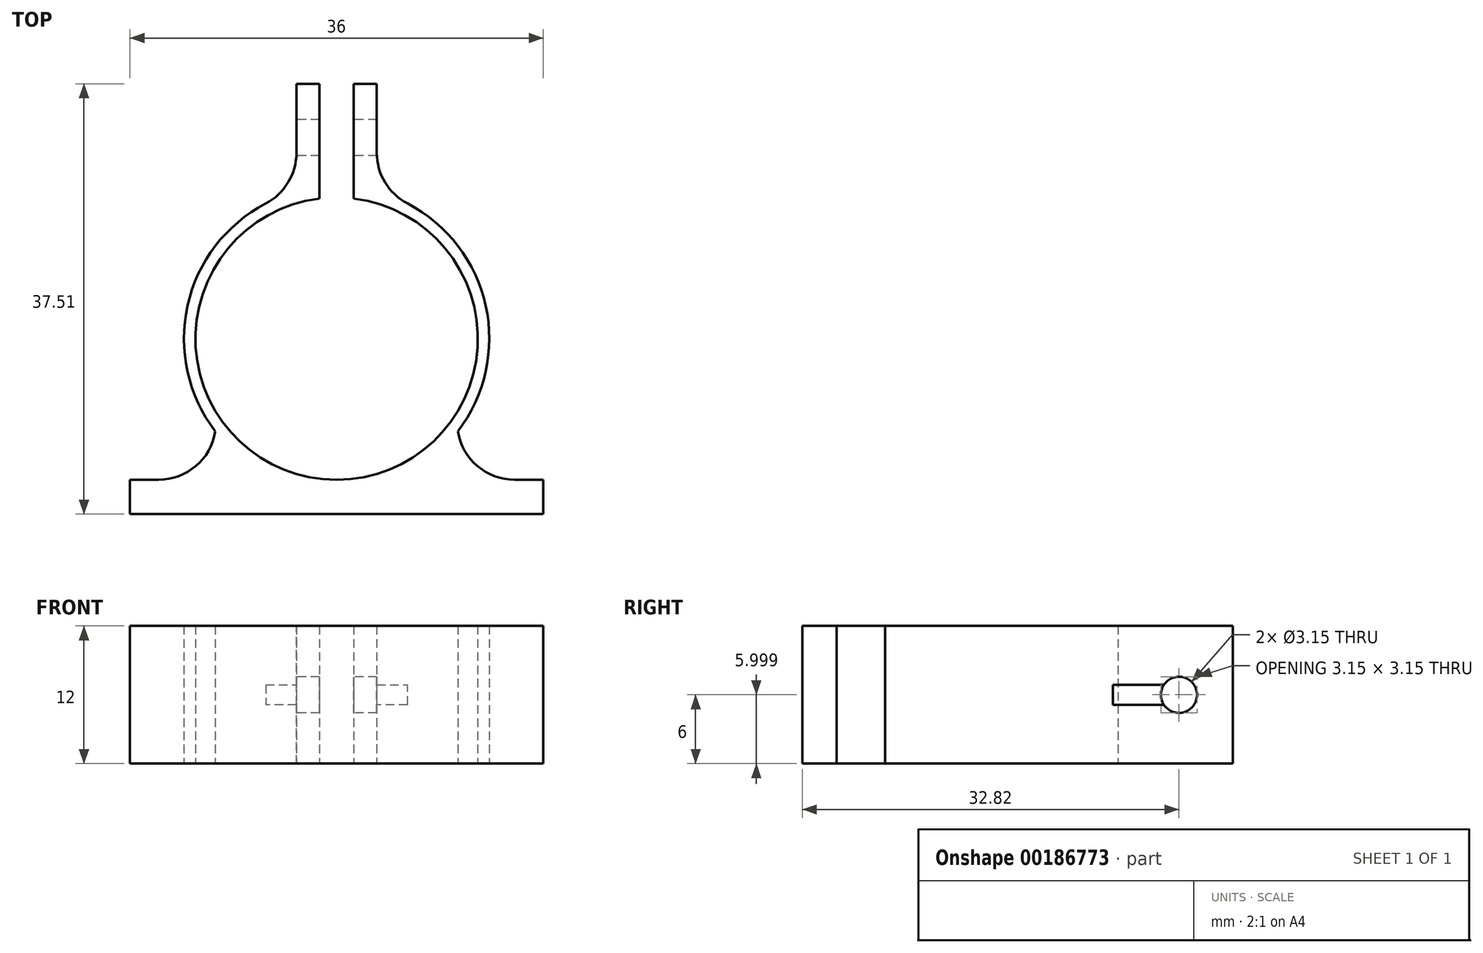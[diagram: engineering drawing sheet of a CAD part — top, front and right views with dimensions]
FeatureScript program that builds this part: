
annotation { "Feature Type Name" : "Feature", "Feature Type Description" : "" }
export const myFeature = defineFeature(function(context is Context, id is Id, definition is map)
    precondition{}
    {
        {
            var Q0;
            Q0=qCreatedBy(makeId("Top.planeOp"),FACE);
            var sketch = newSketch(context, id + "F0", { "sketchPlane" : qUnion([Q0])});
            skCircle(sketch, "E0", {"center": v(0, 0) * mm, "radius": 12.3 * mm});
            skLineSegment(sketch, "E1.bottom", {"start": v(0, -12.3) * mm, "end": v(18, -12.3) * mm});
            skLineSegment(sketch, "E1.top", {"start": v(0, -15.3) * mm, "end": v(18, -15.3) * mm});
            skLineSegment(sketch, "E1.right", {"start": v(18, -12.3) * mm, "end": v(18, -15.3) * mm});
            skLineSegment(sketch, "E2.bottom", {"start": v(0, -12.3) * mm, "end": v(-18, -12.3) * mm});
            skLineSegment(sketch, "E2.top", {"start": v(0, -15.3) * mm, "end": v(-18, -15.3) * mm});
            skLineSegment(sketch, "E2.right", {"start": v(-18, -12.3) * mm, "end": v(-18, -15.3) * mm});
            skCircle(sketch, "E3", {"center": v(0, 0) * mm, "radius": 13.3 * mm});
            skLineSegment(sketch, "E4", {"start": v(-10.56, -12.3) * mm, "end": v(-10.56, -6.3) * mm});
            skLineSegment(sketch, "E5", {"start": v(10.56, -12.3) * mm, "end": v(10.56, -6.3) * mm});
            skLineSegment(sketch, "E6", {"start": v(0, 29.14) * mm, "end": v(0, 0) * mm, "construction": true});
            skLineSegment(sketch, "E7.bottom", {"start": v(1.5, 22.2) * mm, "end": v(-1.5, 22.2) * mm, "construction": true});
            skLineSegment(sketch, "E7.left", {"start": v(1.5, 22.2) * mm, "end": v(1.5, 12.2) * mm});
            skLineSegment(sketch, "E7.right", {"start": v(-1.5, 22.2) * mm, "end": v(-1.5, 12.2) * mm});
            skPoint(sketch, "E7.middle", {"position": v(0, 13.3) * mm});
            skLineSegment(sketch, "E8.bottom", {"start": v(-1.5, 22.2) * mm, "end": v(-3.5, 22.2) * mm});
            skLineSegment(sketch, "E8.top", {"start": v(-1.5, 12.2) * mm, "end": v(-3.5, 12.2) * mm});
            skLineSegment(sketch, "E8.right", {"start": v(-3.5, 22.2) * mm, "end": v(-3.5, 12.2) * mm});
            skLineSegment(sketch, "E9.bottom", {"start": v(1.5, 22.2) * mm, "end": v(3.5, 22.2) * mm});
            skLineSegment(sketch, "E9.top", {"start": v(1.5, 12.2) * mm, "end": v(3.5, 12.2) * mm});
            skLineSegment(sketch, "E9.right", {"start": v(3.5, 22.2) * mm, "end": v(3.5, 12.2) * mm});
            skLineSegment(sketch, "E10", {"start": v(0, 0) * mm, "end": v(0, -22.28) * mm, "construction": true});
            skSolve(sketch);
        }
        {
            var Q0;
            {var subQ0=sQuery(id+"F0.wireOp",EDGE,"E8.top");Q0=makeQuery(id+"F0.imprint","IMPRINT",FACE,{"disambiguationData":[TD([[makeQuery(id+"F0.imprint","IMPRINT",EDGE,{"derivedFrom":subQ0}),1.0]])]});}
            var Q1;
            {var subQ5=sQuery(id+"F0.wireOp",EDGE,"E8.bottom");Q1=makeQuery(id+"F0.imprint","IMPRINT",FACE,{"disambiguationData":[TD([[makeQuery(id+"F0.imprint","IMPRINT",EDGE,{"derivedFrom":subQ5}),1.0]])]});}
            var Q2;
            {var subQ5=sQuery(id+"F0.wireOp",EDGE,"E8.top");Q2=makeQuery(id+"F0.imprint","IMPRINT",FACE,{"disambiguationData":[TD([[makeQuery(id+"F0.imprint","IMPRINT",EDGE,{"derivedFrom":subQ5}),-1.0]])]});}
            var Q3;
            {var subQ5=sQuery(id+"F0.wireOp",EDGE,"E9.bottom");Q3=makeQuery(id+"F0.imprint","IMPRINT",FACE,{"disambiguationData":[TD([[makeQuery(id+"F0.imprint","IMPRINT",EDGE,{"derivedFrom":subQ5}),-1.0]])]});}
            var Q4;
            {var subQ5=sQuery(id+"F0.wireOp",EDGE,"E9.top");Q4=makeQuery(id+"F0.imprint","IMPRINT",FACE,{"disambiguationData":[TD([[makeQuery(id+"F0.imprint","IMPRINT",EDGE,{"derivedFrom":subQ5}),1.0]])]});}
            var Q5;
            {var subQ5=sQuery(id+"F0.wireOp",EDGE,"E9.top");Q5=makeQuery(id+"F0.imprint","IMPRINT",FACE,{"disambiguationData":[TD([[makeQuery(id+"F0.imprint","IMPRINT",EDGE,{"derivedFrom":subQ5}),-1.0]])]});}
            var Q6;
            {var subQ3=sQuery(id+"F0.wireOp",EDGE,"E4");var subQ5=sQuery(id+"F0.wireOp",EDGE,"E3");var subQ7=makeQuery(id+"F0.imprint","INTERSECT",VERTEX,{"derivedFrom":[subQ5,subQ3]});Q6=makeQuery(id+"F0.imprint","IMPRINT",FACE,{"disambiguationData":[TD([[makeQuery(id+"F0.imprint","IMPRINT",EDGE,{"disambiguationData":[TD([[subQ7,-1.0]])],"derivedFrom":subQ5}),1.0]])]});}
            var Q7;
            {var subQ1=sQuery(id+"F0.wireOp",EDGE,"E1.bottom");var subQ3=sQuery(id+"F0.wireOp",EDGE,"E3");var subQ4=makeQuery(id+"F0.imprint","INTERSECT",VERTEX,{"derivedFrom":[subQ1,subQ3]});Q7=makeQuery(id+"F0.imprint","IMPRINT",FACE,{"disambiguationData":[TD([[makeQuery(id+"F0.imprint","IMPRINT",EDGE,{"disambiguationData":[TD([[subQ4,1.0]])],"derivedFrom":subQ3}),1.0]])]});}
            var Q8;
            {var subQ3=sQuery(id+"F0.wireOp",EDGE,"E5");var subQ5=sQuery(id+"F0.wireOp",EDGE,"E3");var subQ7=makeQuery(id+"F0.imprint","INTERSECT",VERTEX,{"derivedFrom":[subQ5,subQ3]});Q8=makeQuery(id+"F0.imprint","IMPRINT",FACE,{"disambiguationData":[TD([[makeQuery(id+"F0.imprint","IMPRINT",EDGE,{"disambiguationData":[TD([[subQ7,1.0]])],"derivedFrom":subQ5}),1.0]])]});}
            var Q9;
            {var subQ0=sQuery(id+"F0.wireOp",EDGE,"E5");var subQ1=sQuery(id+"F0.wireOp",EDGE,"E1.bottom");var subQ2=makeQuery(id+"F0.imprint","INTERSECT",VERTEX,{"derivedFrom":[subQ1,subQ0]});Q9=makeQuery(id+"F0.imprint","IMPRINT",FACE,{"disambiguationData":[TD([[makeQuery(id+"F0.imprint","IMPRINT",EDGE,{"disambiguationData":[TD([[subQ2,1.0]])],"derivedFrom":subQ1}),1.0]])]});}
            var Q10;
            {var subQ0=sQuery(id+"F0.wireOp",EDGE,"E4");var subQ1=sQuery(id+"F0.wireOp",EDGE,"E2.bottom");var subQ2=makeQuery(id+"F0.imprint","INTERSECT",VERTEX,{"derivedFrom":[subQ1,subQ0]});Q10=makeQuery(id+"F0.imprint","IMPRINT",FACE,{"disambiguationData":[TD([[makeQuery(id+"F0.imprint","IMPRINT",EDGE,{"disambiguationData":[TD([[subQ2,1.0]])],"derivedFrom":subQ1}),-1.0]])]});}
            var Q11;
            Q11=makeQuery(id+"F0.imprint","IMPRINT",FACE,{"disambiguationData":[TD([[makeQuery(id+"F0.imprint","IMPRINT",EDGE,{"derivedFrom":sQuery(id+"F0.wireOp",EDGE,"E1.top")}),1.0]])]});
            extrude(context, id + "F1", {"entities" : qUnion([Q0, Q1, Q2, Q3, Q4, Q5, Q6, Q7, Q8, Q9, Q10, Q11]), "depth" : 12 * mm});
        }
        {
            var Q0;
            Q0=makeQuery(id+"F1.opExtrude","SWEPT_FACE",FACE,{"disambiguationData":[OSD([sQuery(id+"F0.wireOp",EDGE,"E8.right")])]});
            var sketch = newSketch(context, id + "F2", { "sketchPlane" : qUnion([Q0])});
            skLineSegment(sketch, "E11", {"start": v(-22.2, 12) * mm, "end": v(-12.83, 0) * mm, "construction": true});
            skPoint(sketch, "E12", {"position": v(-17.52, 6) * mm});
            skSolve(sketch);
        }
        {
            var Q0;
            Q0=sQuery(id+"F2.wireOp",VERTEX,"E12");
            var Q1;
            Q1=makeQuery(id+"F1.opExtrude","SWEPT_BODY",BODY,{"disambiguationData":[OSD([sQuery(id+"F0.wireOp",EDGE,"E0"),sQuery(id+"F0.wireOp",EDGE,"E1.bottom"),sQuery(id+"F0.wireOp",EDGE,"E1.top"),sQuery(id+"F0.wireOp",EDGE,"E1.right"),sQuery(id+"F0.wireOp",EDGE,"E2.bottom"),sQuery(id+"F0.wireOp",EDGE,"E2.top"),sQuery(id+"F0.wireOp",EDGE,"E2.right"),sQuery(id+"F0.wireOp",EDGE,"E3"),sQuery(id+"F0.wireOp",EDGE,"E4"),sQuery(id+"F0.wireOp",EDGE,"E5"),sQuery(id+"F0.wireOp",EDGE,"E8.bottom"),sQuery(id+"F0.wireOp",EDGE,"E7.right"),sQuery(id+"F0.wireOp",EDGE,"E8.right"),sQuery(id+"F0.wireOp",EDGE,"E9.bottom"),sQuery(id+"F0.wireOp",EDGE,"E7.left"),sQuery(id+"F0.wireOp",EDGE,"E9.right")])]});
            hole(context, id + "F3", {"style" : HoleStyle.SIMPLE, "endStyle" : HoleEndStyle.THROUGH, "holeDiameter" : 3.15 * mm, "startFromSketch" : true, "locations" : qUnion([Q0]), "scope" : qUnion([Q1]), "isTappedThrough" : true});
        }
        {
            var Q0;
            Q0=makeQuery(id+"F1.opExtrude","SWEPT_EDGE",EDGE,{"disambiguationData":[OSD([sQuery(id+"F0.wireOp",EDGE,"E1.bottom"),sQuery(id+"F0.wireOp",EDGE,"E5")])]});
            var Q1;
            Q1=makeQuery(id+"F1.opExtrude","SWEPT_EDGE",EDGE,{"disambiguationData":[OSD([sQuery(id+"F0.wireOp",EDGE,"E2.bottom"),sQuery(id+"F0.wireOp",EDGE,"E4")])]});
            var Q2;
            Q2=makeQuery(id+"F1.opExtrude","SWEPT_EDGE",EDGE,{"disambiguationData":[OSD([sQuery(id+"F0.wireOp",EDGE,"E3"),sQuery(id+"F0.wireOp",EDGE,"E9.right")])]});
            var Q3;
            Q3=makeQuery(id+"F1.opExtrude","SWEPT_EDGE",EDGE,{"disambiguationData":[OSD([sQuery(id+"F0.wireOp",EDGE,"E3"),sQuery(id+"F0.wireOp",EDGE,"E8.right")])]});
            fillet(context, id + "F4", {"entities" : qUnion([Q0, Q1, Q2, Q3]), "radius" : 5 * mm, "tangentPropagation" : true, "allowEdgeOverflow" : false});
        }
    });
